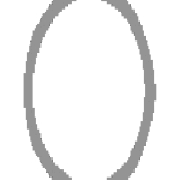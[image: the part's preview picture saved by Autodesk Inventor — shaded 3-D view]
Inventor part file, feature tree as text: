
AUTODESK INVENTOR PART (.ipt)
format: ipt  version: 2021 (Build 250183000, 183)  size: 111,616 bytes
history: native  units: in
note: dims shown in document units (in); Inventor stores cm internally (conversion verified against a paired STEP export)
features: other x4, sketch x3, plane x1
ambient origin geometry x8: Origin, YZ Plane, XZ Plane, XY Plane, X Axis, Y Axis, Z Axis, Center Point
bodies: Solid1 (feature_tree), Body (feature_tree)
feature tree (8):
  other  "Driven Length"
  other  "Frame Generator"
  other  "Start Plane"
  other  "End Plane"
  sketch  "Sketch"  dims[d2=38.7943in d4=-0.0in d5=38.7943in d6=0.12in d7=0.0in d8=90.0deg d9=38.7943in]
  sketch  "Sketch2"  dims[d0=1.0in]
  plane  "Work Plane3"
  sketch  "Sketch3"  dims[d1=0.065in]
